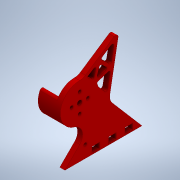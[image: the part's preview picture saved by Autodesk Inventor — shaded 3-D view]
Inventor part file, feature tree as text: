
AUTODESK INVENTOR PART (.ipt)
format: ipt  version: 2020 (Build 240168000, 168)  size: 419,840 bytes
history: native  units: mm
features: extrude x7, sketch x7, other x3, fillet x2, projected_geometry x1
ambient origin geometry x8: Origin, YZ Plane, XZ Plane, XY Plane, X Axis, Y Axis, Z Axis, Center Point
bodies: Solid1 (feature_tree)
feature tree (20):
  other  "WeaponMountBasePlateV1.ipt"
  extrude  "Extrusion1"  Depth=27.8mm
  extrude  "Extrusion2"  Depth=0.5mm
  extrude  "Extrusion3"  Depth=4.5mm
  extrude  "Extrusion4"  Depth=16.0mm
  fillet  "Fillet1"  Radius=3.1mm
  extrude  "Extrusion5"  Depth=19.0mm
  fillet  "Fillet3"  Radius=3.1mm
  extrude  "Extrusion6"  TaperAngle=0.0deg  [1 undecoded]
  extrude  "Extrusion7"  TaperAngle=0.0deg  [1 undecoded]
  other  "Solid1::WeaponMountBasePlateV1.ipt"
  other  "TaggingFeature1"
  sketch  "Sketch2"  dims[d0=10.0mm d2=27.8mm]
  sketch  "Sketch3"  dims[d3=5.0mm d4=0.5mm]
  sketch  "Sketch4"  dims[d5=17.0mm d6=0.0mm d7=4.5mm]
  sketch  "Sketch6"  dims[d8=17.0mm d9=0.0mm d10=16.0mm d11=3.1mm]
  sketch  "Sketch8"  dims[d12=3.1mm d13=19.0mm d14=3.1mm]
  sketch  "Sketch9"  dims[d15=3.1mm d16=0.0mm d17=0.0mm]
  sketch  "Sketch10"  dims[d18=180.0deg d19=0.0mm d20=4.363323mm d21=17.0mm d22=0.0mm d23=10.0mm d25=2.5mm d27=15.0mm d28=8.0mm d29=0.0mm d30=1.0mm d31=13.0mm d32=3.0mm d33=5.0mm d34=7.0mm d35=0.0mm d36=2.0mm d37=1.5mm d38=2.0mm d39=1.5mm d40=61.487mm d41=0.0mm]
  projected_geometry  "Projected Loop1"
note: 2 required parameter values undecoded (feature->parameter linkage not recoverable at this tier; creation-order binding heuristic only, values carry confidence <= 0.55)
